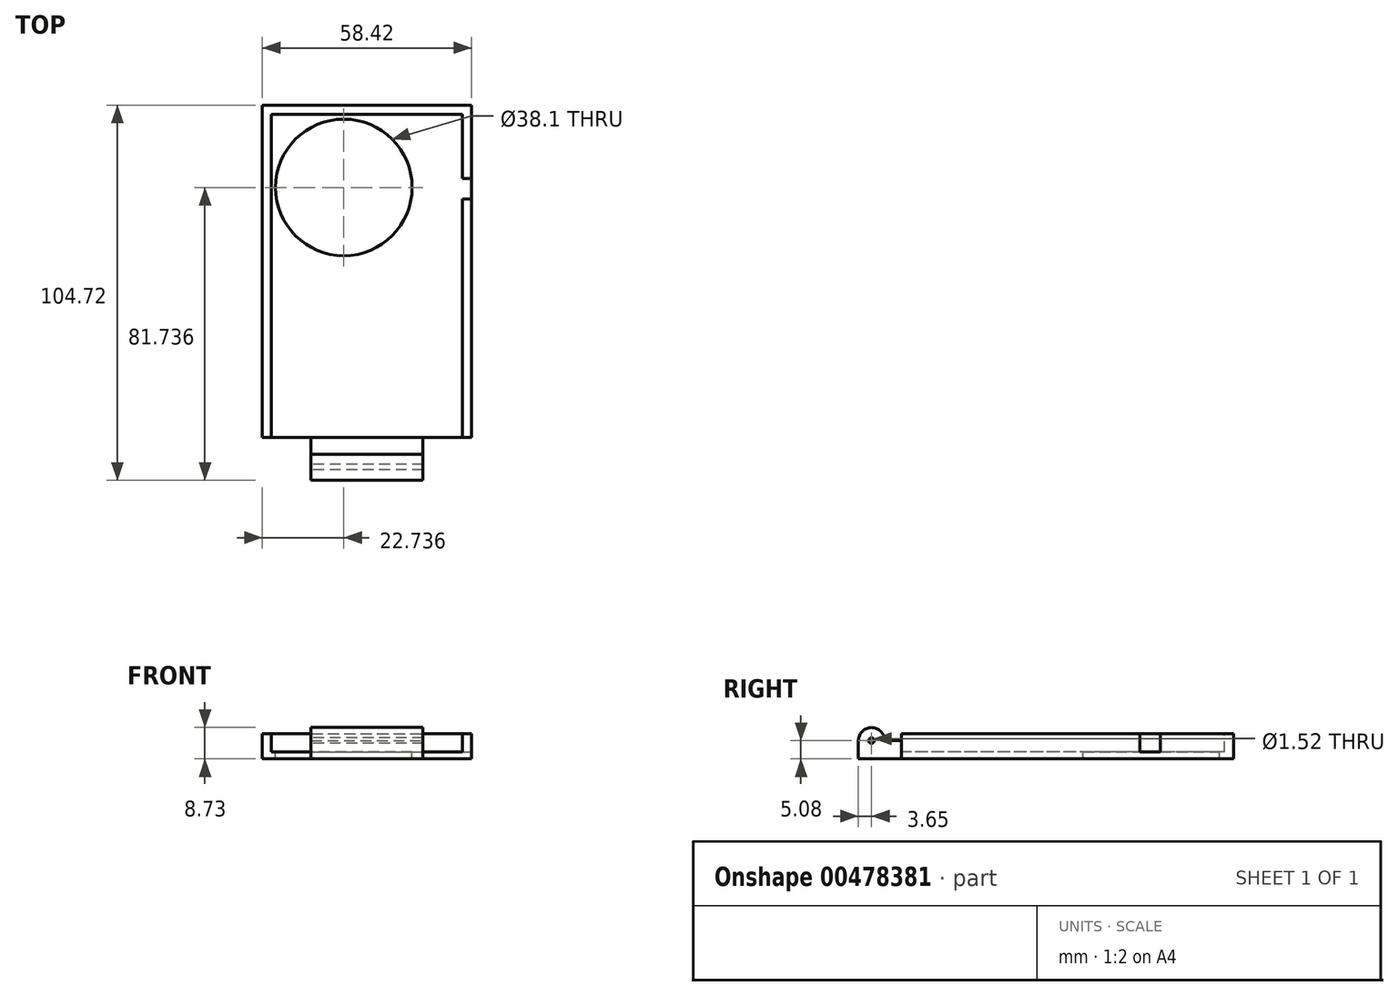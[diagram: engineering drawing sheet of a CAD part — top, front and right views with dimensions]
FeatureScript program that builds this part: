
annotation { "Feature Type Name" : "Feature", "Feature Type Description" : "" }
export const myFeature = defineFeature(function(context is Context, id is Id, definition is map)
    precondition{}
    {
        {
            var Q0;
            Q0=qCreatedBy(makeId("Top.planeOp"),FACE);
            var sketch = newSketch(context, id + "F0", { "sketchPlane" : qUnion([Q0])});
            skLineSegment(sketch, "E0.bottom", {"start": v(-23.42, 55.45) * mm, "end": v(35, 55.45) * mm});
            skLineSegment(sketch, "E0.top", {"start": v(-23.42, -37.26) * mm, "end": v(35, -37.26) * mm});
            skLineSegment(sketch, "E0.left", {"start": v(-23.42, 55.45) * mm, "end": v(-23.42, -37.26) * mm});
            skLineSegment(sketch, "E0.right", {"start": v(35, 55.45) * mm, "end": v(35, -37.26) * mm});
            skSolve(sketch);
        }
        {
            var Q0;
            Q0=makeQuery(id+"F0.imprint","IMPRINT",FACE,{"disambiguationData":[TD([[makeQuery(id+"F0.imprint","IMPRINT",EDGE,{"derivedFrom":sQuery(id+"F0.wireOp",EDGE,"E0.bottom")}),-1.0]])]});
            extrude(context, id + "F1", {"entities" : qUnion([Q0]), "depth" : 7 * mm});
        }
        {
            var Q0;
            Q0=makeQuery(id+"F1.opExtrude","CAP_FACE",FACE,{"disambiguationData":[OSD([sQuery(id+"F0.wireOp",EDGE,"E0.bottom"),sQuery(id+"F0.wireOp",EDGE,"E0.top"),sQuery(id+"F0.wireOp",EDGE,"E0.left"),sQuery(id+"F0.wireOp",EDGE,"E0.right")])],"isStart":false});
            var sketch = newSketch(context, id + "F2", { "sketchPlane" : qUnion([Q0])});
            skLineSegment(sketch, "E1.bottom", {"start": v(-20.88, 52.91) * mm, "end": v(32.46, 52.91) * mm});
            skLineSegment(sketch, "E1.top", {"start": v(-20.88, -37.26) * mm, "end": v(32.46, -37.26) * mm});
            skLineSegment(sketch, "E1.left", {"start": v(-20.88, 52.91) * mm, "end": v(-20.88, -37.26) * mm});
            skLineSegment(sketch, "E1.right", {"start": v(32.46, 52.91) * mm, "end": v(32.46, -37.26) * mm});
            skSolve(sketch);
        }
        {
            var Q0;
            Q0=makeQuery(id+"F2.imprint","IMPRINT",FACE,{"disambiguationData":[TD([[makeQuery(id+"F2.imprint","IMPRINT",EDGE,{"derivedFrom":sQuery(id+"F2.wireOp",EDGE,"E1.bottom")}),-1.0]])]});
            extrude(context, id + "F3", {"entities" : qUnion([Q0]), "operationType" : NewBodyOperationType.REMOVE, "oppositeDirection" : true, "depth" : 5.08 * mm});
        }
        {
            var Q0;
            Q0=makeQuery(id+"F3.boolean.opBoolean","COPY",FACE,{"derivedFrom":makeQuery(id+"F3.opExtrude","CAP_FACE",FACE,{"disambiguationData":[OSD([sQuery(id+"F2.wireOp",EDGE,"E1.bottom"),sQuery(id+"F2.wireOp",EDGE,"E1.top"),sQuery(id+"F2.wireOp",EDGE,"E1.left"),sQuery(id+"F2.wireOp",EDGE,"E1.right")])],"isStart":false})});
            var sketch = newSketch(context, id + "F4", { "sketchPlane" : qUnion([Q0])});
            skCircle(sketch, "E2", {"center": v(-0.68, 32.47) * mm, "radius": 19.05 * mm});
            skSolve(sketch);
        }
        {
            var Q0;
            Q0=makeQuery(id+"F4.imprint","IMPRINT",FACE,{"disambiguationData":[TD([[makeQuery(id+"F4.imprint","IMPRINT",EDGE,{"derivedFrom":sQuery(id+"F4.wireOp",EDGE,"E2")}),1.0]])]});
            extrude(context, id + "F5", {"entities" : qUnion([Q0]), "operationType" : NewBodyOperationType.REMOVE, "oppositeDirection" : true, "depth" : 25.4 * mm});
        }
        {
            var Q0;
            Q0=makeQuery(id+"F1.opExtrude","CAP_FACE",FACE,{"disambiguationData":[OSD([sQuery(id+"F0.wireOp",EDGE,"E0.bottom"),sQuery(id+"F0.wireOp",EDGE,"E0.top"),sQuery(id+"F0.wireOp",EDGE,"E0.left"),sQuery(id+"F0.wireOp",EDGE,"E0.right")])],"isStart":true});
            var sketch = newSketch(context, id + "F6", { "sketchPlane" : qUnion([Q0])});
            skLineSegment(sketch, "E3.bottom", {"start": v(-9.83, 49.27) * mm, "end": v(21.41, 49.27) * mm});
            skLineSegment(sketch, "E3.top", {"start": v(-9.83, 33.88) * mm, "end": v(21.41, 33.88) * mm});
            skLineSegment(sketch, "E3.left", {"start": v(-9.83, 49.27) * mm, "end": v(-9.83, 33.88) * mm});
            skLineSegment(sketch, "E3.right", {"start": v(21.41, 49.27) * mm, "end": v(21.41, 33.88) * mm});
            skSolve(sketch);
        }
        {
            var Q0;
            {var subQ0=sQuery(id+"F6.wireOp",EDGE,"E3.bottom");Q0=makeQuery(id+"F6.imprint","IMPRINT",FACE,{"disambiguationData":[TD([[makeQuery(id+"F6.imprint","IMPRINT",EDGE,{"derivedFrom":subQ0}),-1.0]])]});}
            extrude(context, id + "F7", {"entities" : qUnion([Q0]), "operationType" : NewBodyOperationType.ADD, "oppositeDirection" : true, "depth" : 5.08 * mm});
        }
        {
            var Q0;
            Q0=makeQuery(id+"F7.opExtrude","SWEPT_FACE",FACE,{"disambiguationData":[OSD([sQuery(id+"F6.wireOp",EDGE,"E3.left")])]});
            var sketch = newSketch(context, id + "F8", { "sketchPlane" : qUnion([Q0])});
            skCircle(sketch, "E4", {"center": v(45.62, 5.08) * mm, "radius": 3.65 * mm});
            skSolve(sketch);
        }
        {
            var Q0;
            Q0 = qSketchRegion(id + "F8", true);
            extrude(context, id + "F9", {"entities" : qUnion([Q0]), "operationType" : NewBodyOperationType.ADD, "oppositeDirection" : true, "depth" : 31.24 * mm});
        }
        {
            var Q0;
            Q0=makeQuery(id+"F9.boolean.opBoolean","MERGE",FACE,{"derivedFrom":[makeQuery(id+"F7.opExtrude","SWEPT_FACE",FACE,{"disambiguationData":[OSD([sQuery(id+"F6.wireOp",EDGE,"E3.left")])]}),makeQuery(id+"F9.opExtrude","CAP_FACE",FACE,{"disambiguationData":[OSD([sQuery(id+"F8.wireOp",EDGE,"E4")])],"isStart":true})]});
            var sketch = newSketch(context, id + "F10", { "sketchPlane" : qUnion([Q0])});
            skCircle(sketch, "E5", {"center": v(45.62, 5.08) * mm, "radius": 0.76 * mm});
            skSolve(sketch);
        }
        {
            var Q0;
            Q0=makeQuery(id+"F10.imprint","IMPRINT",FACE,{"disambiguationData":[TD([[makeQuery(id+"F10.imprint","IMPRINT",EDGE,{"derivedFrom":sQuery(id+"F10.wireOp",EDGE,"E5")}),1.0]])]});
            extrude(context, id + "F11", {"entities" : qUnion([Q0]), "operationType" : NewBodyOperationType.REMOVE, "oppositeDirection" : true, "depth" : 38.1 * mm});
        }
        {
            var Q0;
            Q0=makeQuery(id+"F1.opExtrude","CAP_FACE",FACE,{"disambiguationData":[OSD([sQuery(id+"F0.wireOp",EDGE,"E0.bottom"),sQuery(id+"F0.wireOp",EDGE,"E0.top"),sQuery(id+"F0.wireOp",EDGE,"E0.left"),sQuery(id+"F0.wireOp",EDGE,"E0.right")])],"isStart":false});
            var sketch = newSketch(context, id + "F12", { "sketchPlane" : qUnion([Q0])});
            skLineSegment(sketch, "E6.bottom", {"start": v(25.4, 35) * mm, "end": v(38.1, 35) * mm});
            skLineSegment(sketch, "E6.top", {"start": v(25.4, 29.3) * mm, "end": v(38.1, 29.3) * mm});
            skLineSegment(sketch, "E6.left", {"start": v(25.4, 35) * mm, "end": v(25.4, 29.3) * mm});
            skLineSegment(sketch, "E6.right", {"start": v(38.1, 35) * mm, "end": v(38.1, 29.3) * mm});
            skSolve(sketch);
        }
        {
            var Q0;
            {var subQ0=sQuery(id+"F12.wireOp",EDGE,"E6.bottom");var subQ1=makeQuery(id+"F3.boolean.opBoolean","COPY",EDGE,{"derivedFrom":makeQuery(id+"F3.opExtrude","CAP_EDGE",EDGE,{"disambiguationData":[OSD([sQuery(id+"F2.wireOp",EDGE,"E1.right")])],"isStart":true})});var subQ2=makeQuery(id+"F12.imprint","INTERSECT",VERTEX,{"derivedFrom":[subQ1,subQ0]});Q0=makeQuery(id+"F12.imprint","IMPRINT",FACE,{"disambiguationData":[TD([[makeQuery(id+"F12.imprint","IMPRINT",EDGE,{"disambiguationData":[TD([[subQ2,-1.0]])],"derivedFrom":subQ0}),-1.0]])]});}
            extrude(context, id + "F13", {"entities" : qUnion([Q0]), "operationType" : NewBodyOperationType.REMOVE, "oppositeDirection" : true, "depth" : 5.08 * mm});
        }
    });
